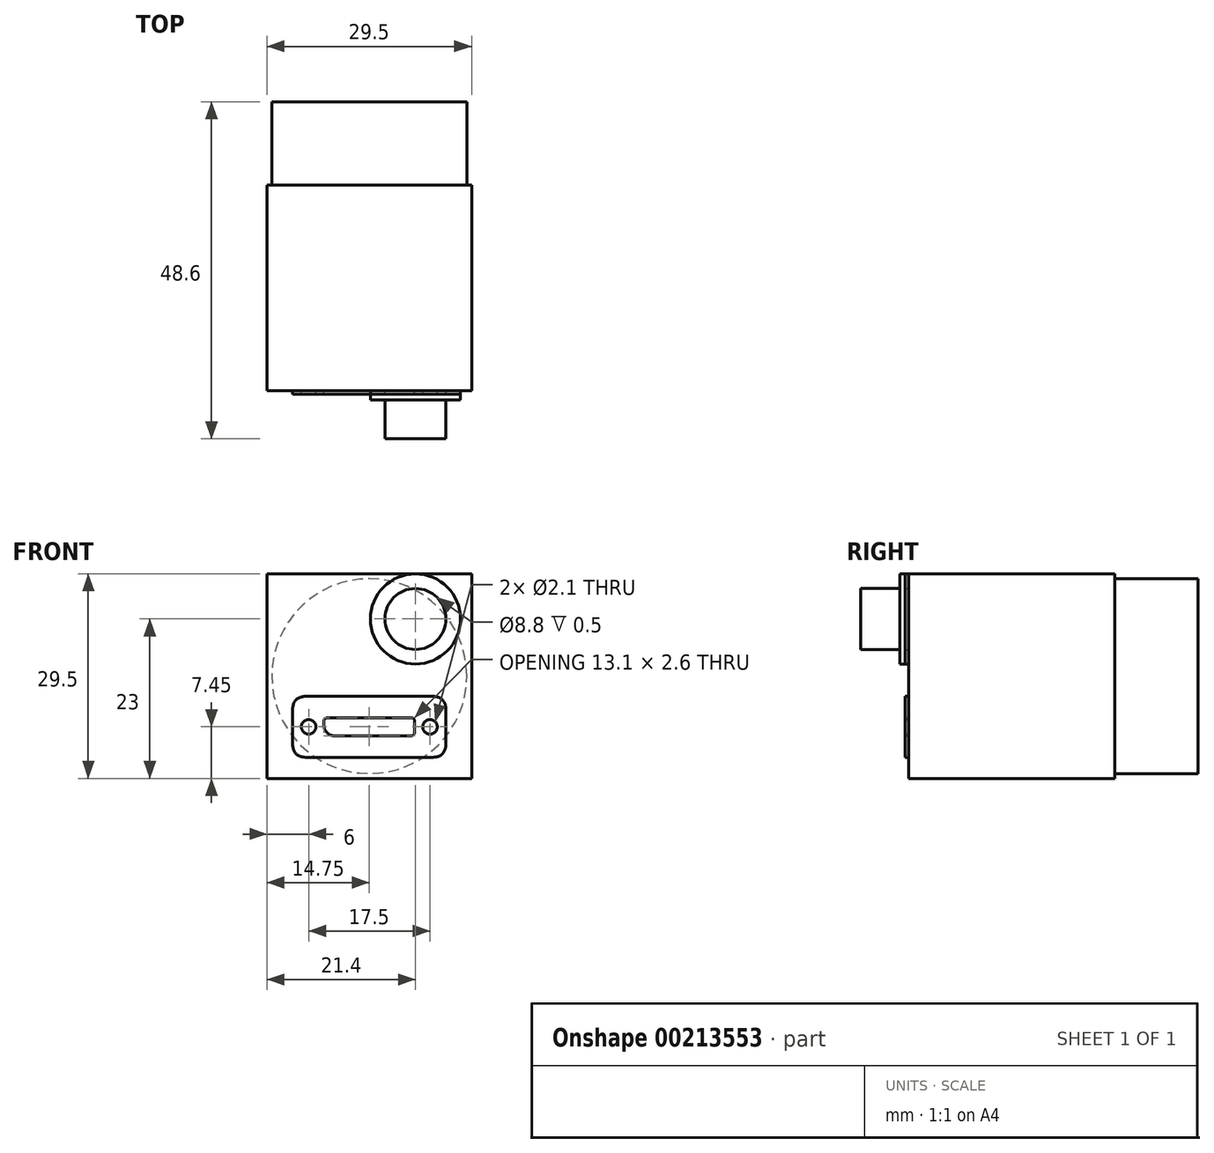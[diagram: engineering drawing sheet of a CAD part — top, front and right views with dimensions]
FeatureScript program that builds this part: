
annotation { "Feature Type Name" : "Feature", "Feature Type Description" : "" }
export const myFeature = defineFeature(function(context is Context, id is Id, definition is map)
    precondition{}
    {
        {
            var Q0;
            Q0=qCreatedBy(makeId("Front.planeOp"),FACE);
            var sketch = newSketch(context, id + "F0", { "sketchPlane" : qUnion([Q0])});
            skCircle(sketch, "E0.cCircle", {"center": v(0, 0) * mm, "radius": 14.75 * mm, "construction": true});
            skLineSegment(sketch, "E0.0", {"start": v(14.75, 14.75) * mm, "end": v(14.75, -14.75) * mm});
            skLineSegment(sketch, "E0.1", {"start": v(14.75, -14.75) * mm, "end": v(-14.75, -14.75) * mm});
            skLineSegment(sketch, "E0.2", {"start": v(-14.75, -14.75) * mm, "end": v(-14.75, 14.75) * mm});
            skLineSegment(sketch, "E0.3", {"start": v(-14.75, 14.75) * mm, "end": v(14.75, 14.75) * mm});
            skPoint(sketch, "E0.0.midPoint", {"position": v(14.75, 0) * mm});
            skCircle(sketch, "E1", {"center": v(0, 0) * mm, "radius": 14.05 * mm});
            skSolve(sketch);
        }
        {
            var Q0;
            Q0=makeQuery(id+"F0.imprint","IMPRINT",FACE,{"disambiguationData":[TD([[makeQuery(id+"F0.imprint","IMPRINT",EDGE,{"derivedFrom":sQuery(id+"F0.wireOp",EDGE,"E1")}),1.0]])]});
            extrude(context, id + "F1", {"entities" : qUnion([Q0]), "oppositeDirection" : true, "depth" : 12 * mm});
        }
        {
            var Q0;
            Q0=makeQuery(id+"F0.imprint","IMPRINT",FACE,{"disambiguationData":[TD([[makeQuery(id+"F0.imprint","IMPRINT",EDGE,{"derivedFrom":sQuery(id+"F0.wireOp",EDGE,"E0.0")}),-1.0]])]});
            extrude(context, id + "F2", {"entities" : qUnion([Q0]), "depth" : 29.7 * mm});
        }
        {
            var Q0;
            Q0=makeQuery(id+"F0.imprint","IMPRINT",FACE,{"disambiguationData":[TD([[makeQuery(id+"F0.imprint","IMPRINT",EDGE,{"derivedFrom":sQuery(id+"F0.wireOp",EDGE,"E1")}),1.0]])]});
            extrude(context, id + "F3", {"entities" : qUnion([Q0]), "depth" : 29.7 * mm});
        }
        {
            var Q0;
            Q0=qCreatedBy(makeId("Front.planeOp"),FACE);
            cPlane(context, id + "F4", {"entities" : qUnion([Q0]), "cplaneType" : CPlaneType.OFFSET, "offset" : 29.7 * mm, "width" : 150 * mm, "height" : 150 * mm});
        }
        {
            var Q0;
            Q0=qCreatedBy(id+"F4.planeOp",FACE);
            var sketch = newSketch(context, id + "F5", { "sketchPlane" : qUnion([Q0])});
            skLineSegment(sketch, "E2", {"start": v(0, 0) * mm, "end": v(0, 8.25) * mm, "construction": true});
            skLineSegment(sketch, "E3", {"start": v(0, 8.25) * mm, "end": v(6.65, 8.25) * mm, "construction": true});
            skLineSegment(sketch, "E4", {"start": v(0, 8.25) * mm, "end": v(0, 14.7) * mm, "construction": true});
            skCircle(sketch, "E5", {"center": v(6.65, 8.25) * mm, "radius": 6.5 * mm});
            skCircle(sketch, "E6", {"center": v(6.65, 8.25) * mm, "radius": 4.4 * mm});
            skLineSegment(sketch, "E7", {"start": v(0, 0) * mm, "end": v(0, -7.3) * mm, "construction": true});
            skLineSegment(sketch, "E8.bottom", {"start": v(-11.05, -11.7) * mm, "end": v(11.05, -11.7) * mm});
            skLineSegment(sketch, "E8.top", {"start": v(-11.05, -2.9) * mm, "end": v(11.05, -2.9) * mm});
            skLineSegment(sketch, "E8.left", {"start": v(-11.05, -11.7) * mm, "end": v(-11.05, -2.9) * mm});
            skLineSegment(sketch, "E8.right", {"start": v(11.05, -11.7) * mm, "end": v(11.05, -2.9) * mm});
            skPoint(sketch, "E8.middle", {"position": v(0, -7.3) * mm});
            skLineSegment(sketch, "E9", {"start": v(0, -7.3) * mm, "end": v(-8.75, -7.3) * mm, "construction": true});
            skLineSegment(sketch, "E10.MirrorCS", {"start": v(0, -7.3) * mm, "end": v(8.75, -7.3) * mm, "construction": true});
            skLineSegment(sketch, "E11.bottom", {"start": v(6.55, -8.6) * mm, "end": v(-6.55, -8.6) * mm});
            skLineSegment(sketch, "E11.top", {"start": v(6.55, -6) * mm, "end": v(-6.55, -6) * mm});
            skLineSegment(sketch, "E11.left", {"start": v(6.55, -8.6) * mm, "end": v(6.55, -6) * mm});
            skLineSegment(sketch, "E11.right", {"start": v(-6.55, -8.6) * mm, "end": v(-6.55, -6) * mm});
            skSolve(sketch);
        }
        {
            var Q0;
            Q0=makeQuery(id+"F5.imprint","IMPRINT",FACE,{"disambiguationData":[TD([[makeQuery(id+"F5.imprint","IMPRINT",EDGE,{"derivedFrom":sQuery(id+"F5.wireOp",EDGE,"E5")}),1.0]])]});
            extrude(context, id + "F6", {"entities" : qUnion([Q0]), "depth" : 1.3 * mm});
        }
        {
            var Q0;
            Q0=makeQuery(id+"F5.imprint","IMPRINT",FACE,{"disambiguationData":[TD([[makeQuery(id+"F5.imprint","IMPRINT",EDGE,{"derivedFrom":sQuery(id+"F5.wireOp",EDGE,"E6")}),1.0]])]});
            extrude(context, id + "F7", {"entities" : qUnion([Q0]), "operationType" : NewBodyOperationType.ADD, "depth" : 6.9 * mm});
        }
        {
            var Q0;
            Q0 = qSketchRegion(id + "F5", true);
            extrude(context, id + "F8", {"entities" : qUnion([Q0]), "depth" : .5 * mm});
        }
        {
            var Q0;
            Q0=makeQuery(id+"F8.opExtrude","SWEPT_EDGE",EDGE,{"disambiguationData":[OSD([sQuery(id+"F5.wireOp",EDGE,"E8.top"),sQuery(id+"F5.wireOp",EDGE,"E8.left")])]});
            var Q1;
            Q1=makeQuery(id+"F8.opExtrude","SWEPT_EDGE",EDGE,{"disambiguationData":[OSD([sQuery(id+"F5.wireOp",EDGE,"E8.top"),sQuery(id+"F5.wireOp",EDGE,"E8.right")])]});
            var Q2;
            Q2=makeQuery(id+"F8.opExtrude","SWEPT_EDGE",EDGE,{"disambiguationData":[OSD([sQuery(id+"F5.wireOp",EDGE,"E8.bottom"),sQuery(id+"F5.wireOp",EDGE,"E8.left")])]});
            var Q3;
            Q3=makeQuery(id+"F8.opExtrude","SWEPT_EDGE",EDGE,{"disambiguationData":[OSD([sQuery(id+"F5.wireOp",EDGE,"E8.bottom"),sQuery(id+"F5.wireOp",EDGE,"E8.right")])]});
            fillet(context, id + "F9", {"entities" : qUnion([Q0, Q1, Q2, Q3]), "radius" : 2 * mm, "tangentPropagation" : true, "rho" : 0.5, "crossSection" : FilletCrossSection.CONIC, "allowEdgeOverflow" : false});
        }
        {
            var Q0;
            Q0=sQuery(id+"F5.wireOp",VERTEX,"E9.end");
            var Q1;
            Q1=sQuery(id+"F5.wireOp",VERTEX,"E10.MirrorCS.end");
            var Q2;
            Q2=makeQuery(id+"F8.opExtrude","SWEPT_BODY",BODY,{"disambiguationData":[OSD([sQuery(id+"F5.wireOp",EDGE,"E8.bottom"),sQuery(id+"F5.wireOp",EDGE,"E8.top"),sQuery(id+"F5.wireOp",EDGE,"E8.left"),sQuery(id+"F5.wireOp",EDGE,"E8.right")])]});
            hole(context, id + "F10", {"style" : HoleStyle.SIMPLE, "endStyle" : HoleEndStyle.THROUGH, "oppositeDirection" : true, "holeDiameter" : 2.1 * mm, "locations" : qUnion([Q0, Q1]), "scope" : qUnion([Q2]), "isTappedThrough" : true});
        }
        {
            var Q0;
            Q0=makeQuery(id+"F8.opExtrude","SWEPT_EDGE",EDGE,{"disambiguationData":[OSD([sQuery(id+"F5.wireOp",EDGE,"E11.top"),sQuery(id+"F5.wireOp",EDGE,"E11.right")])]});
            var Q1;
            Q1=makeQuery(id+"F8.opExtrude","SWEPT_EDGE",EDGE,{"disambiguationData":[OSD([sQuery(id+"F5.wireOp",EDGE,"E11.top"),sQuery(id+"F5.wireOp",EDGE,"E11.left")])]});
            var Q2;
            Q2=makeQuery(id+"F8.opExtrude","SWEPT_EDGE",EDGE,{"disambiguationData":[OSD([sQuery(id+"F5.wireOp",EDGE,"E11.bottom"),sQuery(id+"F5.wireOp",EDGE,"E11.left")])]});
            fillet(context, id + "F11", {"entities" : qUnion([Q0, Q1, Q2]), "radius" : .5 * mm, "tangentPropagation" : true, "allowEdgeOverflow" : false});
        }
        {
            var Q0;
            Q0=makeQuery(id+"F8.opExtrude","SWEPT_EDGE",EDGE,{"disambiguationData":[OSD([sQuery(id+"F5.wireOp",EDGE,"E11.bottom"),sQuery(id+"F5.wireOp",EDGE,"E11.right")])]});
            fillet(context, id + "F12", {"entities" : qUnion([Q0]), "radius" : 1.5 * mm, "tangentPropagation" : true, "allowEdgeOverflow" : false});
        }
    });
